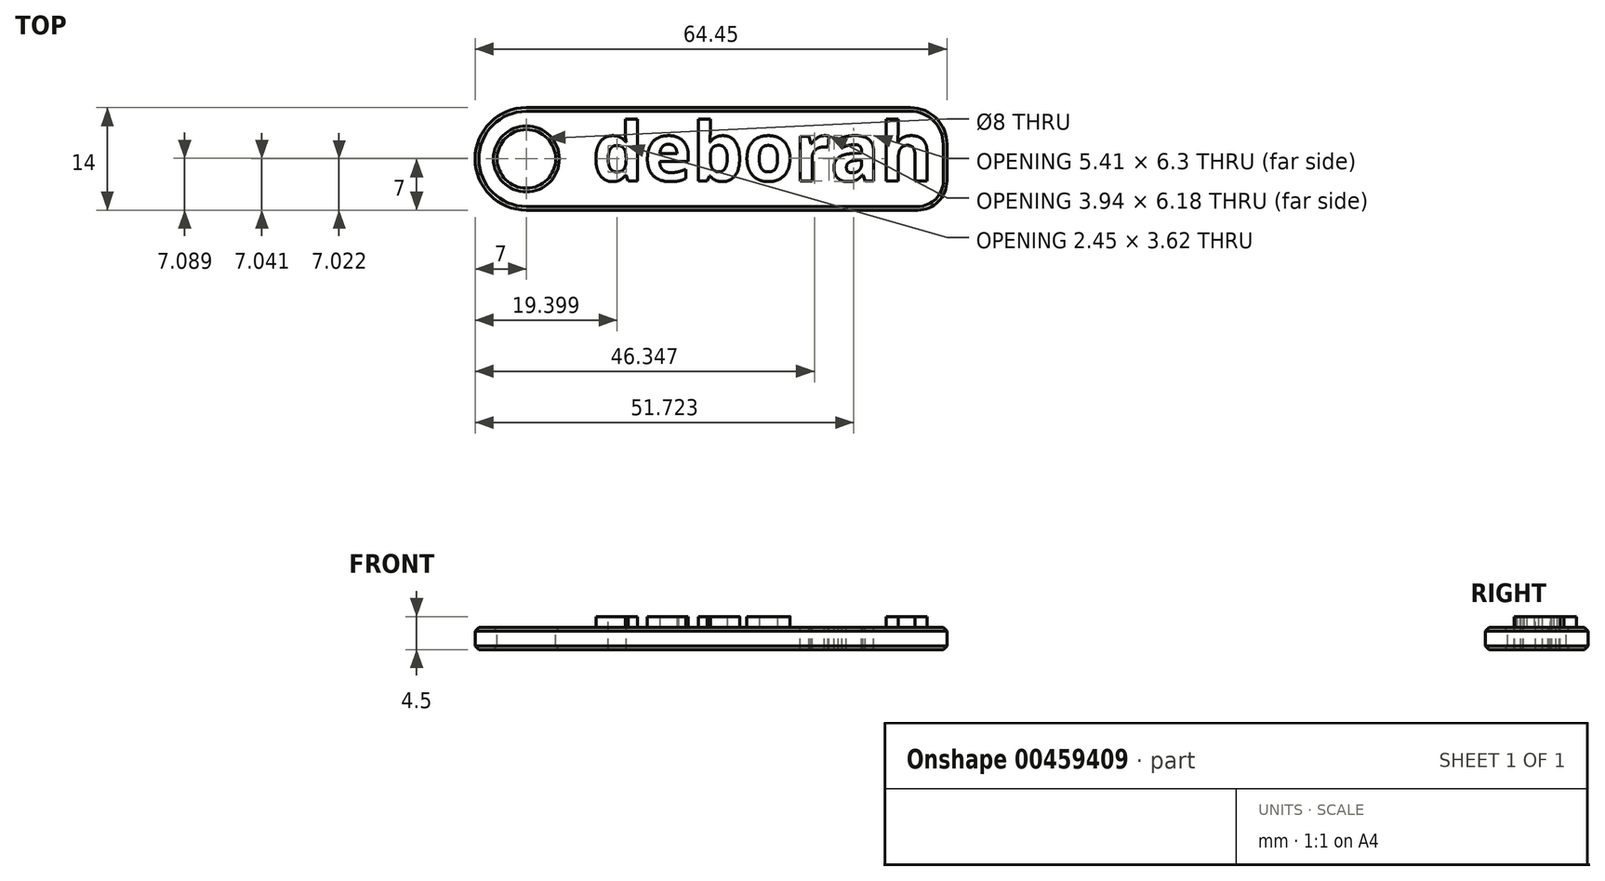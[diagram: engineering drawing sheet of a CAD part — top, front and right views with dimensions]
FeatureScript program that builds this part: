
annotation { "Feature Type Name" : "Feature", "Feature Type Description" : "" }
export const myFeature = defineFeature(function(context is Context, id is Id, definition is map)
    precondition{}
    {
        {
            var Q0;
            Q0=qCreatedBy(makeId("Top.planeOp"),FACE);
            var sketch = newSketch(context, id + "F0", { "sketchPlane" : qUnion([Q0])});
            skCircle(sketch, "E0", {"center": v(0, 0) * mm, "radius": 4 * mm});
            skCircle(sketch, "E1", {"center": v(0, 0) * mm, "radius": 7 * mm});
            skLineSegment(sketch, "E2.bottom", {"start": v(0, 7) * mm, "end": v(52.45, 7) * mm});
            skLineSegment(sketch, "E2.top", {"start": v(0, -7) * mm, "end": v(53.45, -7) * mm});
            skLineSegment(sketch, "E2.left", {"start": v(0, 7) * mm, "end": v(0, -7) * mm});
            skLineSegment(sketch, "E2.right", {"start": v(57.45, 2) * mm, "end": v(57.45, -3) * mm});
            skPoint(sketch, "E3.visualSharp", {"position": v(57.45, 7) * mm});
            skArc(sketch, "E3.filletArc", {"start": v(57.45, 2) * mm, "mid": v(55.99, 5.54) * mm, "end": v(52.45, 7) * mm});
            skPoint(sketch, "E4.visualSharp", {"position": v(57.45, -7) * mm});
            skArc(sketch, "E4.filletArc", {"start": v(53.45, -7) * mm, "mid": v(56.28, -5.83) * mm, "end": v(57.45, -3) * mm});
            skText(sketch, "E5", { "text": "deborah", "fontName": "OpenSans-Bold.ttf"});
            const initialGuessF0  = {"E5": [0.009, -0.003, 1, 0, 0.008]};
            skSetInitialGuess(sketch, initialGuessF0);
            skSolve(sketch);
        }
        {
            var Q0;
            Q0=makeQuery(id+"F0.imprint","IMPRINT",FACE,{"disambiguationData":[TD([[makeQuery(id+"F0.imprint","IMPRINT",EDGE,{"derivedFrom":sQuery(id+"F0.wireOp",EDGE,"E5.sketch_text.stroke-357")}),-1.0]])]});
            var Q1;
            Q1=makeQuery(id+"F0.imprint","IMPRINT",FACE,{"disambiguationData":[TD([[makeQuery(id+"F0.imprint","IMPRINT",EDGE,{"derivedFrom":sQuery(id+"F0.wireOp",EDGE,"E5.sketch_text.stroke-375")}),1.0]])]});
            var Q2;
            Q2=makeQuery(id+"F0.imprint","IMPRINT",FACE,{"disambiguationData":[TD([[makeQuery(id+"F0.imprint","IMPRINT",EDGE,{"derivedFrom":sQuery(id+"F0.wireOp",EDGE,"E5.sketch_text.stroke-382")}),-1.0]])]});
            var Q3;
            Q3=makeQuery(id+"F0.imprint","IMPRINT",FACE,{"disambiguationData":[TD([[makeQuery(id+"F0.imprint","IMPRINT",EDGE,{"derivedFrom":sQuery(id+"F0.wireOp",EDGE,"E5.sketch_text.stroke-410")}),-1.0]])]});
            var Q4;
            Q4=makeQuery(id+"F0.imprint","IMPRINT",FACE,{"disambiguationData":[TD([[makeQuery(id+"F0.imprint","IMPRINT",EDGE,{"derivedFrom":sQuery(id+"F0.wireOp",EDGE,"E5.sketch_text.stroke-428")}),1.0]])]});
            var Q5;
            Q5=makeQuery(id+"F0.imprint","IMPRINT",FACE,{"disambiguationData":[TD([[makeQuery(id+"F0.imprint","IMPRINT",EDGE,{"derivedFrom":sQuery(id+"F0.wireOp",EDGE,"E5.sketch_text.stroke-329")}),-1.0]])]});
            var Q6;
            Q6=makeQuery(id+"F0.imprint","IMPRINT",FACE,{"disambiguationData":[TD([[makeQuery(id+"F0.imprint","IMPRINT",EDGE,{"derivedFrom":sQuery(id+"F0.wireOp",EDGE,"E5.sketch_text.stroke-304")}),-1.0]])]});
            var Q7;
            Q7=makeQuery(id+"F0.imprint","IMPRINT",FACE,{"disambiguationData":[TD([[makeQuery(id+"F0.imprint","IMPRINT",EDGE,{"derivedFrom":sQuery(id+"F0.wireOp",EDGE,"E5.sketch_text.stroke-322")}),1.0]])]});
            var Q8;
            Q8=makeQuery(id+"F0.imprint","IMPRINT",FACE,{"disambiguationData":[TD([[makeQuery(id+"F0.imprint","IMPRINT",EDGE,{"derivedFrom":sQuery(id+"F0.wireOp",EDGE,"E5.sketch_text.stroke-269")}),1.0]])]});
            var Q9;
            Q9=makeQuery(id+"F0.imprint","IMPRINT",FACE,{"disambiguationData":[TD([[makeQuery(id+"F0.imprint","IMPRINT",EDGE,{"derivedFrom":sQuery(id+"F0.wireOp",EDGE,"E5.sketch_text.stroke-216")}),1.0]])]});
            var Q10;
            Q10=makeQuery(id+"F0.imprint","IMPRINT",FACE,{"disambiguationData":[TD([[makeQuery(id+"F0.imprint","IMPRINT",EDGE,{"derivedFrom":sQuery(id+"F0.wireOp",EDGE,"E5.sketch_text.stroke-163")}),1.0]])]});
            var Q11;
            Q11=makeQuery(id+"F0.imprint","IMPRINT",FACE,{"disambiguationData":[TD([[makeQuery(id+"F0.imprint","IMPRINT",EDGE,{"derivedFrom":sQuery(id+"F0.wireOp",EDGE,"E5.sketch_text.stroke-110")}),1.0]])]});
            var Q12;
            Q12=makeQuery(id+"F0.imprint","IMPRINT",FACE,{"disambiguationData":[TD([[makeQuery(id+"F0.imprint","IMPRINT",EDGE,{"derivedFrom":sQuery(id+"F0.wireOp",EDGE,"E5.sketch_text.stroke-18")}),1.0]])]});
            var Q13;
            Q13=makeQuery(id+"F0.imprint","IMPRINT",FACE,{"disambiguationData":[TD([[makeQuery(id+"F0.imprint","IMPRINT",EDGE,{"derivedFrom":sQuery(id+"F0.wireOp",EDGE,"E5.sketch_text.stroke-0")}),-1.0]])]});
            var Q14;
            Q14=makeQuery(id+"F0.imprint","IMPRINT",FACE,{"disambiguationData":[TD([[makeQuery(id+"F0.imprint","IMPRINT",EDGE,{"derivedFrom":sQuery(id+"F0.wireOp",EDGE,"E5.sketch_text.stroke-25")}),-1.0]])]});
            var Q15;
            Q15=makeQuery(id+"F0.imprint","IMPRINT",FACE,{"disambiguationData":[TD([[makeQuery(id+"F0.imprint","IMPRINT",EDGE,{"derivedFrom":sQuery(id+"F0.wireOp",EDGE,"E5.sketch_text.stroke-42")}),-1.0]])]});
            var Q16;
            Q16=makeQuery(id+"F0.imprint","IMPRINT",FACE,{"disambiguationData":[TD([[makeQuery(id+"F0.imprint","IMPRINT",EDGE,{"derivedFrom":sQuery(id+"F0.wireOp",EDGE,"E5.sketch_text.stroke-59")}),-1.0]])]});
            var Q17;
            Q17=makeQuery(id+"F0.imprint","IMPRINT",FACE,{"disambiguationData":[TD([[makeQuery(id+"F0.imprint","IMPRINT",EDGE,{"derivedFrom":sQuery(id+"F0.wireOp",EDGE,"E5.sketch_text.stroke-64")}),-1.0]])]});
            var Q18;
            Q18=makeQuery(id+"F0.imprint","IMPRINT",FACE,{"disambiguationData":[TD([[makeQuery(id+"F0.imprint","IMPRINT",EDGE,{"derivedFrom":sQuery(id+"F0.wireOp",EDGE,"E5.sketch_text.stroke-92")}),-1.0]])]});
            var Q19;
            Q19=makeQuery(id+"F0.imprint","IMPRINT",FACE,{"disambiguationData":[TD([[makeQuery(id+"F0.imprint","IMPRINT",EDGE,{"derivedFrom":sQuery(id+"F0.wireOp",EDGE,"E5.sketch_text.stroke-117")}),-1.0]])]});
            var Q20;
            Q20=makeQuery(id+"F0.imprint","IMPRINT",FACE,{"disambiguationData":[TD([[makeQuery(id+"F0.imprint","IMPRINT",EDGE,{"derivedFrom":sQuery(id+"F0.wireOp",EDGE,"E5.sketch_text.stroke-145")}),-1.0]])]});
            var Q21;
            Q21=makeQuery(id+"F0.imprint","IMPRINT",FACE,{"disambiguationData":[TD([[makeQuery(id+"F0.imprint","IMPRINT",EDGE,{"derivedFrom":sQuery(id+"F0.wireOp",EDGE,"E5.sketch_text.stroke-170")}),-1.0]])]});
            var Q22;
            Q22=makeQuery(id+"F0.imprint","IMPRINT",FACE,{"disambiguationData":[TD([[makeQuery(id+"F0.imprint","IMPRINT",EDGE,{"derivedFrom":sQuery(id+"F0.wireOp",EDGE,"E5.sketch_text.stroke-198")}),-1.0]])]});
            var Q23;
            Q23=makeQuery(id+"F0.imprint","IMPRINT",FACE,{"disambiguationData":[TD([[makeQuery(id+"F0.imprint","IMPRINT",EDGE,{"derivedFrom":sQuery(id+"F0.wireOp",EDGE,"E5.sketch_text.stroke-223")}),-1.0]])]});
            var Q24;
            Q24=makeQuery(id+"F0.imprint","IMPRINT",FACE,{"disambiguationData":[TD([[makeQuery(id+"F0.imprint","IMPRINT",EDGE,{"derivedFrom":sQuery(id+"F0.wireOp",EDGE,"E5.sketch_text.stroke-251")}),-1.0]])]});
            var Q25;
            Q25=makeQuery(id+"F0.imprint","IMPRINT",FACE,{"disambiguationData":[TD([[makeQuery(id+"F0.imprint","IMPRINT",EDGE,{"derivedFrom":sQuery(id+"F0.wireOp",EDGE,"E5.sketch_text.stroke-276")}),-1.0]])]});
            var Q26;
            {var subQ1=sQuery(id+"F0.wireOp",EDGE,"E2.bottom");Q26=makeQuery(id+"F0.imprint","IMPRINT",FACE,{"disambiguationData":[TD([[makeQuery(id+"F0.imprint","IMPRINT",EDGE,{"derivedFrom":subQ1}),-1.0]])]});}
            var Q27;
            {var subQ0=sQuery(id+"F0.wireOp",EDGE,"E2.left");var subQ1=sQuery(id+"F0.wireOp",EDGE,"E0");var subQ2=makeQuery(id+"F0.imprint","INTERSECT",VERTEX,{"disambiguationData":[OD(0.0)],"derivedFrom":[subQ1,subQ0]});Q27=makeQuery(id+"F0.imprint","IMPRINT",FACE,{"disambiguationData":[TD([[makeQuery(id+"F0.imprint","IMPRINT",EDGE,{"disambiguationData":[TD([[subQ2,-1.0]])],"derivedFrom":subQ1}),-1.0]])]});}
            var Q28;
            {var subQ0=sQuery(id+"F0.wireOp",EDGE,"E2.left");var subQ1=sQuery(id+"F0.wireOp",EDGE,"E0");var subQ2=makeQuery(id+"F0.imprint","INTERSECT",VERTEX,{"disambiguationData":[OD(0.0)],"derivedFrom":[subQ1,subQ0]});Q28=makeQuery(id+"F0.imprint","IMPRINT",FACE,{"disambiguationData":[TD([[makeQuery(id+"F0.imprint","IMPRINT",EDGE,{"disambiguationData":[TD([[subQ2,1.0]])],"derivedFrom":subQ1}),-1.0]])]});}
            var Q29;
            Q29=makeQuery(id+"F0.imprint","IMPRINT",FACE,{"disambiguationData":[TD([[makeQuery(id+"F0.imprint","IMPRINT",EDGE,{"derivedFrom":sQuery(id+"F0.wireOp",EDGE,"E5.sketch_text.stroke-5")}),-1.0]])]});
            var Q30;
            Q30=makeQuery(id+"F0.imprint","IMPRINT",FACE,{"disambiguationData":[TD([[makeQuery(id+"F0.imprint","IMPRINT",EDGE,{"derivedFrom":sQuery(id+"F0.wireOp",EDGE,"E5.sketch_text.stroke-53")}),1.0]])]});
            var Q31;
            Q31=makeQuery(id+"F0.imprint","IMPRINT",FACE,{"disambiguationData":[TD([[makeQuery(id+"F0.imprint","IMPRINT",EDGE,{"derivedFrom":sQuery(id+"F0.wireOp",EDGE,"E5.sketch_text.stroke-78")}),1.0]])]});
            var Q32;
            Q32=makeQuery(id+"F0.imprint","IMPRINT",FACE,{"disambiguationData":[TD([[makeQuery(id+"F0.imprint","IMPRINT",EDGE,{"derivedFrom":sQuery(id+"F0.wireOp",EDGE,"E5.sketch_text.stroke-23")}),1.0]])]});
            var Q33;
            Q33=makeQuery(id+"F0.imprint","IMPRINT",FACE,{"disambiguationData":[TD([[makeQuery(id+"F0.imprint","IMPRINT",EDGE,{"derivedFrom":sQuery(id+"F0.wireOp",EDGE,"E5.sketch_text.stroke-57")}),1.0]])]});
            var Q34;
            Q34=makeQuery(id+"F0.imprint","IMPRINT",FACE,{"disambiguationData":[TD([[makeQuery(id+"F0.imprint","IMPRINT",EDGE,{"derivedFrom":sQuery(id+"F0.wireOp",EDGE,"E5.sketch_text.stroke-66")}),-1.0]])]});
            var Q35;
            Q35=makeQuery(id+"F0.imprint","IMPRINT",FACE,{"disambiguationData":[TD([[makeQuery(id+"F0.imprint","IMPRINT",EDGE,{"derivedFrom":sQuery(id+"F0.wireOp",EDGE,"E5.sketch_text.stroke-66")}),1.0]])]});
            var Q36;
            Q36=makeQuery(id+"F0.imprint","IMPRINT",FACE,{"disambiguationData":[TD([[makeQuery(id+"F0.imprint","IMPRINT",EDGE,{"derivedFrom":sQuery(id+"F0.wireOp",EDGE,"E5.sketch_text.stroke-115")}),1.0]])]});
            var Q37;
            Q37=makeQuery(id+"F0.imprint","IMPRINT",FACE,{"disambiguationData":[TD([[makeQuery(id+"F0.imprint","IMPRINT",EDGE,{"derivedFrom":sQuery(id+"F0.wireOp",EDGE,"E5.sketch_text.stroke-122")}),-1.0]])]});
            extrude(context, id + "F1", {"entities" : qUnion([Q0, Q1, Q2, Q3, Q4, Q5, Q6, Q7, Q8, Q9, Q10, Q11, Q12, Q13, Q14, Q15, Q16, Q17, Q18, Q19, Q20, Q21, Q22, Q23, Q24, Q25, Q26, Q27, Q28, Q29, Q30, Q31, Q32, Q33, Q34, Q35, Q36, Q37]), "oppositeDirection" : true, "depth" : 3 * mm, "offsetDistance" : 25 * mm});
        }
        {
            var Q0;
            Q0=makeQuery(id+"F0.imprint","IMPRINT",FACE,{"disambiguationData":[TD([[makeQuery(id+"F0.imprint","IMPRINT",EDGE,{"derivedFrom":sQuery(id+"F0.wireOp",EDGE,"E5.sketch_text.stroke-10")}),-1.0]])]});
            var Q1;
            Q1=makeQuery(id+"F0.imprint","IMPRINT",FACE,{"disambiguationData":[TD([[makeQuery(id+"F0.imprint","IMPRINT",EDGE,{"derivedFrom":sQuery(id+"F0.wireOp",EDGE,"E5.sketch_text.stroke-0")}),-1.0]])]});
            var Q2;
            Q2=makeQuery(id+"F0.imprint","IMPRINT",FACE,{"disambiguationData":[TD([[makeQuery(id+"F0.imprint","IMPRINT",EDGE,{"derivedFrom":sQuery(id+"F0.wireOp",EDGE,"E5.sketch_text.stroke-15")}),-1.0]])]});
            var Q3;
            Q3=makeQuery(id+"F0.imprint","IMPRINT",FACE,{"disambiguationData":[TD([[makeQuery(id+"F0.imprint","IMPRINT",EDGE,{"derivedFrom":sQuery(id+"F0.wireOp",EDGE,"E5.sketch_text.stroke-33")}),-1.0]])]});
            var Q4;
            Q4=makeQuery(id+"F0.imprint","IMPRINT",FACE,{"disambiguationData":[TD([[makeQuery(id+"F0.imprint","IMPRINT",EDGE,{"derivedFrom":sQuery(id+"F0.wireOp",EDGE,"E5.sketch_text.stroke-59")}),-1.0]])]});
            var Q5;
            Q5=makeQuery(id+"F0.imprint","IMPRINT",FACE,{"disambiguationData":[TD([[makeQuery(id+"F0.imprint","IMPRINT",EDGE,{"derivedFrom":sQuery(id+"F0.wireOp",EDGE,"E5.sketch_text.stroke-42")}),-1.0]])]});
            var Q6;
            Q6=makeQuery(id+"F0.imprint","IMPRINT",FACE,{"disambiguationData":[TD([[makeQuery(id+"F0.imprint","IMPRINT",EDGE,{"derivedFrom":sQuery(id+"F0.wireOp",EDGE,"E5.sketch_text.stroke-64")}),-1.0]])]});
            var Q7;
            Q7=makeQuery(id+"F0.imprint","IMPRINT",FACE,{"disambiguationData":[TD([[makeQuery(id+"F0.imprint","IMPRINT",EDGE,{"derivedFrom":sQuery(id+"F0.wireOp",EDGE,"E5.sketch_text.stroke-92")}),-1.0]])]});
            var Q8;
            Q8=makeQuery(id+"F0.imprint","IMPRINT",FACE,{"disambiguationData":[TD([[makeQuery(id+"F0.imprint","IMPRINT",EDGE,{"derivedFrom":sQuery(id+"F0.wireOp",EDGE,"E5.sketch_text.stroke-117")}),-1.0]])]});
            var Q9;
            Q9=makeQuery(id+"F0.imprint","IMPRINT",FACE,{"disambiguationData":[TD([[makeQuery(id+"F0.imprint","IMPRINT",EDGE,{"derivedFrom":sQuery(id+"F0.wireOp",EDGE,"E5.sketch_text.stroke-145")}),-1.0]])]});
            var Q10;
            Q10=makeQuery(id+"F0.imprint","IMPRINT",FACE,{"disambiguationData":[TD([[makeQuery(id+"F0.imprint","IMPRINT",EDGE,{"derivedFrom":sQuery(id+"F0.wireOp",EDGE,"E5.sketch_text.stroke-170")}),-1.0]])]});
            var Q11;
            Q11=makeQuery(id+"F0.imprint","IMPRINT",FACE,{"disambiguationData":[TD([[makeQuery(id+"F0.imprint","IMPRINT",EDGE,{"derivedFrom":sQuery(id+"F0.wireOp",EDGE,"E5.sketch_text.stroke-198")}),-1.0]])]});
            var Q12;
            Q12=makeQuery(id+"F0.imprint","IMPRINT",FACE,{"disambiguationData":[TD([[makeQuery(id+"F0.imprint","IMPRINT",EDGE,{"derivedFrom":sQuery(id+"F0.wireOp",EDGE,"E5.sketch_text.stroke-223")}),-1.0]])]});
            var Q13;
            Q13=makeQuery(id+"F0.imprint","IMPRINT",FACE,{"disambiguationData":[TD([[makeQuery(id+"F0.imprint","IMPRINT",EDGE,{"derivedFrom":sQuery(id+"F0.wireOp",EDGE,"E5.sketch_text.stroke-251")}),-1.0]])]});
            var Q14;
            Q14=makeQuery(id+"F0.imprint","IMPRINT",FACE,{"disambiguationData":[TD([[makeQuery(id+"F0.imprint","IMPRINT",EDGE,{"derivedFrom":sQuery(id+"F0.wireOp",EDGE,"E5.sketch_text.stroke-276")}),-1.0]])]});
            var Q15;
            Q15=makeQuery(id+"F0.imprint","IMPRINT",FACE,{"disambiguationData":[TD([[makeQuery(id+"F0.imprint","IMPRINT",EDGE,{"derivedFrom":sQuery(id+"F0.wireOp",EDGE,"E5.sketch_text.stroke-304")}),-1.0]])]});
            var Q16;
            Q16=makeQuery(id+"F0.imprint","IMPRINT",FACE,{"disambiguationData":[TD([[makeQuery(id+"F0.imprint","IMPRINT",EDGE,{"derivedFrom":sQuery(id+"F0.wireOp",EDGE,"E5.sketch_text.stroke-329")}),-1.0]])]});
            var Q17;
            Q17=makeQuery(id+"F0.imprint","IMPRINT",FACE,{"disambiguationData":[TD([[makeQuery(id+"F0.imprint","IMPRINT",EDGE,{"derivedFrom":sQuery(id+"F0.wireOp",EDGE,"E5.sketch_text.stroke-357")}),-1.0]])]});
            var Q18;
            Q18=makeQuery(id+"F0.imprint","IMPRINT",FACE,{"disambiguationData":[TD([[makeQuery(id+"F0.imprint","IMPRINT",EDGE,{"derivedFrom":sQuery(id+"F0.wireOp",EDGE,"E5.sketch_text.stroke-382")}),-1.0]])]});
            var Q19;
            Q19=makeQuery(id+"F0.imprint","IMPRINT",FACE,{"disambiguationData":[TD([[makeQuery(id+"F0.imprint","IMPRINT",EDGE,{"derivedFrom":sQuery(id+"F0.wireOp",EDGE,"E5.sketch_text.stroke-410")}),-1.0]])]});
            var Q20;
            Q20=makeQuery(id+"F0.imprint","IMPRINT",FACE,{"disambiguationData":[TD([[makeQuery(id+"F0.imprint","IMPRINT",EDGE,{"derivedFrom":sQuery(id+"F0.wireOp",EDGE,"E5.sketch_text.stroke-5")}),-1.0]])]});
            var Q21;
            Q21=makeQuery(id+"F0.imprint","IMPRINT",FACE,{"disambiguationData":[TD([[makeQuery(id+"F0.imprint","IMPRINT",EDGE,{"derivedFrom":sQuery(id+"F0.wireOp",EDGE,"E5.sketch_text.stroke-122")}),-1.0]])]});
            var Q22;
            Q22=makeQuery(id+"F0.imprint","IMPRINT",FACE,{"disambiguationData":[TD([[makeQuery(id+"F0.imprint","IMPRINT",EDGE,{"derivedFrom":sQuery(id+"F0.wireOp",EDGE,"E5.sketch_text.stroke-66")}),-1.0]])]});
            extrude(context, id + "F2", {"entities" : qUnion([Q0, Q1, Q2, Q3, Q4, Q5, Q6, Q7, Q8, Q9, Q10, Q11, Q12, Q13, Q14, Q15, Q16, Q17, Q18, Q19, Q20, Q21, Q22]), "operationType" : NewBodyOperationType.ADD, "depth" : 1.5 * mm, "offsetDistance" : 25 * mm});
        }
        {
            var Q0;
            Q0=makeQuery(id+"F1.opExtrude","CAP_EDGE",EDGE,{"disambiguationData":[OSD([sQuery(id+"F0.wireOp",EDGE,"E0")])],"isStart":true});
            var Q1;
            Q1=makeQuery(id+"F1.opExtrude","CAP_EDGE",EDGE,{"disambiguationData":[OSD([sQuery(id+"F0.wireOp",EDGE,"E2.right")])],"isStart":true});
            var Q2;
            Q2=makeQuery(id+"F1.opExtrude","CAP_EDGE",EDGE,{"disambiguationData":[OSD([sQuery(id+"F0.wireOp",EDGE,"E2.right")])],"isStart":false});
            var Q3;
            Q3=makeQuery(id+"F1.opExtrude","CAP_EDGE",EDGE,{"disambiguationData":[OSD([sQuery(id+"F0.wireOp",EDGE,"E0")])],"isStart":false});
            chamfer(context, id + "F3", {"entities" : qUnion([Q0, Q1, Q2, Q3]), "width" : 0.5 * mm, "tangentPropagation" : true});
        }
    });
